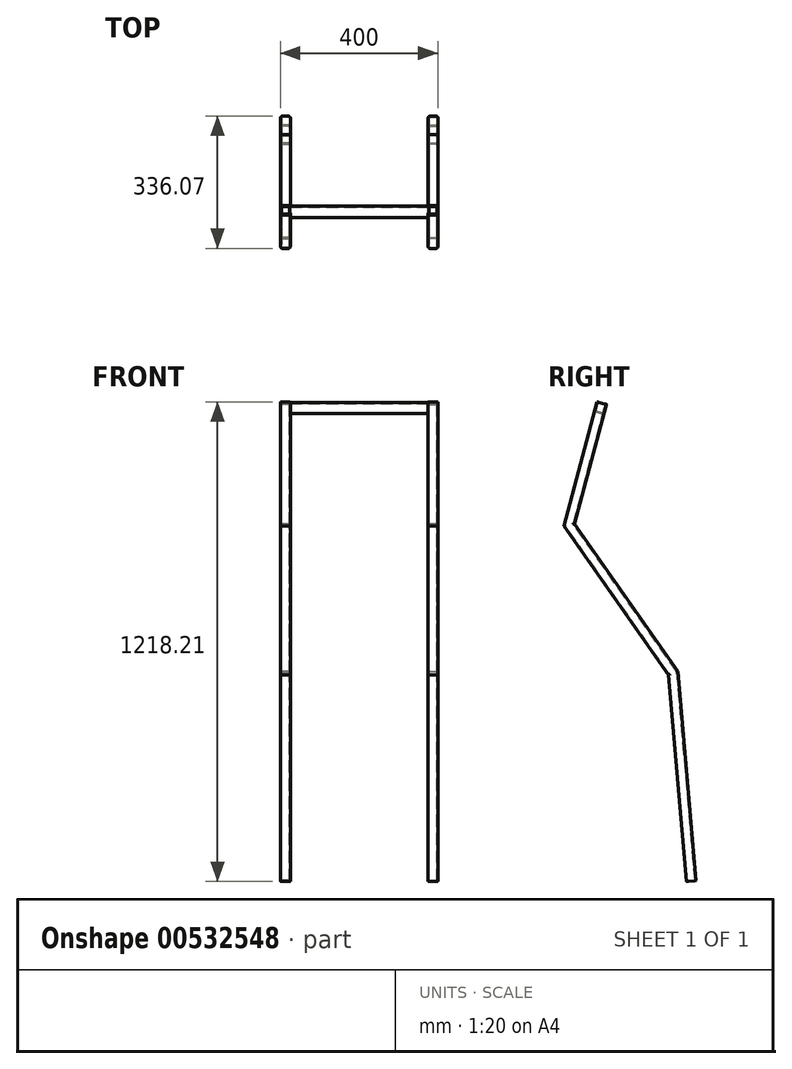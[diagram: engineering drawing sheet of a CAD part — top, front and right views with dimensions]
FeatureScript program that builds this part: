
annotation { "Feature Type Name" : "Feature", "Feature Type Description" : "" }
export const myFeature = defineFeature(function(context is Context, id is Id, definition is map)
    precondition{}
    {
        {
            var Q0;
            Q0=qCreatedBy(makeId("Right.planeOp"),FACE);
            var sketch = newSketch(context, id + "F0", { "sketchPlane" : qUnion([Q0])});
            skLineSegment(sketch, "E0", {"start": v(-227.22, 1213.89) * mm, "end": v(-310.04, 904.8) * mm});
            skLineSegment(sketch, "E1", {"start": v(-310.04, 904.8) * mm, "end": v(-46.2, 527.98) * mm});
            skLineSegment(sketch, "E2", {"start": v(-46.2, 527.98) * mm, "end": v(0, 0) * mm});
            skSolve(sketch);
        }
        {
            var Q0;
            Q0=sQuery(id+"F0.wireOp",EDGE,"E2");
            var Q1;
            Q1=sQuery(id+"F0.wireOp",VERTEX,"E2.end");
            cPlane(context, id + "F1", {"entities" : qUnion([Q0, Q1]), "cplaneType" : CPlaneType.LINE_POINT, "offset" : 25 * mm, "width" : 150 * mm, "height" : 150 * mm});
        }
        {
            var Q0;
            Q0=qCreatedBy(id+"F1.planeOp",FACE);
            var sketch = newSketch(context, id + "F2", { "sketchPlane" : qUnion([Q0])});
            skLineSegment(sketch, "E3.bottom", {"start": v(-7.5, -12.5) * mm, "end": v(7.5, -12.5) * mm});
            skLineSegment(sketch, "E3.top", {"start": v(-7.5, 12.5) * mm, "end": v(7.5, 12.5) * mm});
            skLineSegment(sketch, "E3.left", {"start": v(-12.5, -7.5) * mm, "end": v(-12.5, 7.5) * mm});
            skLineSegment(sketch, "E3.right", {"start": v(12.5, -7.5) * mm, "end": v(12.5, 7.5) * mm});
            skPoint(sketch, "E3.middle", {"position": v(0, 0) * mm});
            skPoint(sketch, "E4.visualSharp", {"position": v(12.5, 12.5) * mm});
            skArc(sketch, "E4.filletArc", {"start": v(12.5, 7.5) * mm, "mid": v(11.04, 11.04) * mm, "end": v(7.5, 12.5) * mm});
            skPoint(sketch, "E5.visualSharp", {"position": v(12.5, -12.5) * mm});
            skArc(sketch, "E5.filletArc", {"start": v(7.5, -12.5) * mm, "mid": v(11.04, -11.04) * mm, "end": v(12.5, -7.5) * mm});
            skPoint(sketch, "E6.visualSharp", {"position": v(-12.5, -12.5) * mm});
            skArc(sketch, "E6.filletArc", {"start": v(-12.5, -7.5) * mm, "mid": v(-11.04, -11.04) * mm, "end": v(-7.5, -12.5) * mm});
            skPoint(sketch, "E7.visualSharp", {"position": v(-12.5, 12.5) * mm});
            skArc(sketch, "E7.filletArc", {"start": v(-7.5, 12.5) * mm, "mid": v(-11.04, 11.04) * mm, "end": v(-12.5, 7.5) * mm});
            skArc(sketch, "E8.0", {"start": v(7.5, -10) * mm, "mid": v(9.27, -9.27) * mm, "end": v(10, -7.5) * mm});
            skLineSegment(sketch, "E8.1", {"start": v(-7.5, -10) * mm, "end": v(7.5, -10) * mm});
            skLineSegment(sketch, "E8.2", {"start": v(10, -7.5) * mm, "end": v(10, 7.5) * mm});
            skArc(sketch, "E8.3", {"start": v(-10, -7.5) * mm, "mid": v(-9.27, -9.27) * mm, "end": v(-7.5, -10) * mm});
            skArc(sketch, "E8.4", {"start": v(10, 7.5) * mm, "mid": v(9.27, 9.27) * mm, "end": v(7.5, 10) * mm});
            skLineSegment(sketch, "E8.5", {"start": v(-7.5, 10) * mm, "end": v(7.5, 10) * mm});
            skArc(sketch, "E8.6", {"start": v(-7.5, 10) * mm, "mid": v(-9.27, 9.27) * mm, "end": v(-10, 7.5) * mm});
            skLineSegment(sketch, "E8.7", {"start": v(-10, -7.5) * mm, "end": v(-10, 7.5) * mm});
            skSolve(sketch);
        }
        {
            var Q0;
            Q0 = qSketchRegion(id + "F2", true);
            var Q1;
            Q1=sQuery(id+"F0.wireOp",EDGE,"E2");
            var Q2;
            Q2=sQuery(id+"F0.wireOp",EDGE,"E1");
            var Q3;
            Q3=sQuery(id+"F0.wireOp",EDGE,"E0");
            sweep(context, id + "F3", {"profiles" : qUnion([Q0]), "path" : qUnion([Q1, Q2, Q3])});
        }
        {
            var Q0;
            Q0=makeQuery(id+"F3.opSweep","SWEPT_FACE",FACE,{"disambiguationData":[OSD([sQuery(id+"F0.wireOp",EDGE,"E2"),sQuery(id+"F2.wireOp",EDGE,"E3.left")])]});
            var sketch = newSketch(context, id + "F4", { "sketchPlane" : qUnion([Q0])});
            skLineSegment(sketch, "E9", {"start": v(219.97, 1211.95) * mm, "end": v(234.46, 1215.83) * mm});
            skLineSegment(sketch, "E10", {"start": v(240.58, 1212.3) * mm, "end": v(244.47, 1197.8) * mm});
            skLineSegment(sketch, "E11", {"start": v(240.93, 1191.68) * mm, "end": v(226.44, 1187.8) * mm});
            skLineSegment(sketch, "E12", {"start": v(220.32, 1191.34) * mm, "end": v(216.44, 1205.82) * mm});
            skPoint(sketch, "E13.visualSharp", {"position": v(215.14, 1210.65) * mm});
            skArc(sketch, "E13.filletArc", {"start": v(219.97, 1211.95) * mm, "mid": v(216.94, 1209.62) * mm, "end": v(216.44, 1205.82) * mm});
            skPoint(sketch, "E14.visualSharp", {"position": v(239.29, 1217.12) * mm});
            skArc(sketch, "E14.filletArc", {"start": v(240.58, 1212.3) * mm, "mid": v(238.25, 1215.33) * mm, "end": v(234.46, 1215.83) * mm});
            skPoint(sketch, "E15.visualSharp", {"position": v(245.76, 1192.98) * mm});
            skArc(sketch, "E15.filletArc", {"start": v(240.93, 1191.68) * mm, "mid": v(243.97, 1194.01) * mm, "end": v(244.47, 1197.8) * mm});
            skPoint(sketch, "E16.visualSharp", {"position": v(221.61, 1186.5) * mm});
            skArc(sketch, "E16.filletArc", {"start": v(220.32, 1191.34) * mm, "mid": v(222.65, 1188.3) * mm, "end": v(226.44, 1187.8) * mm});
            skLineSegment(sketch, "E17.0", {"start": v(238.17, 1211.65) * mm, "end": v(242.05, 1197.16) * mm});
            skArc(sketch, "E17.1", {"start": v(240.28, 1194.1) * mm, "mid": v(241.8, 1195.26) * mm, "end": v(242.05, 1197.16) * mm});
            skArc(sketch, "E17.2", {"start": v(238.17, 1211.65) * mm, "mid": v(237, 1213.17) * mm, "end": v(235.1, 1213.42) * mm});
            skLineSegment(sketch, "E17.3", {"start": v(240.28, 1194.1) * mm, "end": v(225.8, 1190.21) * mm});
            skLineSegment(sketch, "E17.4", {"start": v(220.62, 1209.53) * mm, "end": v(235.1, 1213.42) * mm});
            skArc(sketch, "E17.5", {"start": v(220.62, 1209.53) * mm, "mid": v(219.1, 1208.37) * mm, "end": v(218.85, 1206.47) * mm});
            skLineSegment(sketch, "E17.6", {"start": v(222.73, 1191.98) * mm, "end": v(218.85, 1206.47) * mm});
            skArc(sketch, "E17.7", {"start": v(222.73, 1191.98) * mm, "mid": v(223.9, 1190.46) * mm, "end": v(225.8, 1190.21) * mm});
            skSolve(sketch);
        }
        {
            var Q0;
            Q0 = qSketchRegion(id + "F4", true);
            extrude(context, id + "F5", {"entities" : qUnion([Q0]), "operationType" : NewBodyOperationType.ADD, "depth" : 175 * mm, "offsetDistance" : 25 * mm});
        }
        {
            var Q0;
            Q0=makeQuery(id+"F3.opSweep","SWEPT_BODY",BODY,{"disambiguationData":[OSD([sQuery(id+"F0.wireOp",EDGE,"E0"),sQuery(id+"F2.wireOp",EDGE,"E3.bottom"),sQuery(id+"F2.wireOp",EDGE,"E3.top"),sQuery(id+"F2.wireOp",EDGE,"E3.left"),sQuery(id+"F2.wireOp",EDGE,"E3.right"),sQuery(id+"F2.wireOp",EDGE,"E4.filletArc"),sQuery(id+"F2.wireOp",EDGE,"E5.filletArc"),sQuery(id+"F2.wireOp",EDGE,"E6.filletArc"),sQuery(id+"F2.wireOp",EDGE,"E7.filletArc"),sQuery(id+"F2.wireOp",EDGE,"E8.0"),sQuery(id+"F2.wireOp",EDGE,"E8.1"),sQuery(id+"F2.wireOp",EDGE,"E8.2"),sQuery(id+"F2.wireOp",EDGE,"E8.3"),sQuery(id+"F2.wireOp",EDGE,"E8.4"),sQuery(id+"F2.wireOp",EDGE,"E8.5"),sQuery(id+"F2.wireOp",EDGE,"E8.6"),sQuery(id+"F2.wireOp",EDGE,"E8.7")])]});
            var Q1;
            Q1=makeQuery(id+"F5.opExtrude","CAP_FACE",FACE,{"disambiguationData":[OSD([sQuery(id+"F4.wireOp",EDGE,"E9"),sQuery(id+"F4.wireOp",EDGE,"E10"),sQuery(id+"F4.wireOp",EDGE,"E11"),sQuery(id+"F4.wireOp",EDGE,"E12"),sQuery(id+"F4.wireOp",EDGE,"E13.filletArc"),sQuery(id+"F4.wireOp",EDGE,"E14.filletArc"),sQuery(id+"F4.wireOp",EDGE,"E15.filletArc"),sQuery(id+"F4.wireOp",EDGE,"E16.filletArc"),sQuery(id+"F4.wireOp",EDGE,"E17.0"),sQuery(id+"F4.wireOp",EDGE,"E17.1"),sQuery(id+"F4.wireOp",EDGE,"E17.2"),sQuery(id+"F4.wireOp",EDGE,"E17.3"),sQuery(id+"F4.wireOp",EDGE,"E17.4"),sQuery(id+"F4.wireOp",EDGE,"E17.5"),sQuery(id+"F4.wireOp",EDGE,"E17.6"),sQuery(id+"F4.wireOp",EDGE,"E17.7")])],"isStart":false});
            mirror(context, id + "F6", {"operationType" : NewBodyOperationType.ADD, "entities" : qUnion([Q0]), "mirrorPlane" : qUnion([Q1])});
        }
    });
